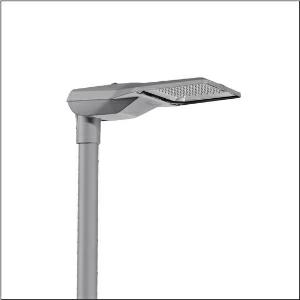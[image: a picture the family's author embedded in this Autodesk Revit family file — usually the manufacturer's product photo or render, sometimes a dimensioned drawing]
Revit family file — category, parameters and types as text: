
# Revit family: streetlight_sl_21_midi___pl52_5xe3h33s08lb_2890
name_source: partatom
category: Lighting Fixtures
units: mm (PartAtom-declared; Revit-internal decimal feet)

## family parameters
Cut with Voids When Loaded = No
Host = Face
Light Source = No
Part Type = Normal
Room Calculation Point = No
Round Connector Dimension = Use Diameter
Shared = No

## types (1)
- --- (1 x LED, 14100 lm, 98.3 W, 3000K)
    Apparent Load = 98 VA
    CIE Flux Codes = 27 59 98 100 100
    Color Rendering = 70
    Color Temperature = 3000K
    Default Elevation = 1800 mm
    Description = Streetlight SL 21 midi, mast luminaire, primary light control with lens, of PMMA, primary optical cover: cover, of toughened safety glass, transparent, light distribution: PL52, light emission: direct distribution, primary light characteristic: asymmetric, installation type: side-entry, post-top, LED, High Power LED, rated luminous flux: 14.100lm, luminous efficacy: 143lm/W, light colour: 730, colour temperature: 3000K, control: overheat protection, constant luminous flux control, time-dependent luminous flux control, flexible luminous flux parameterisation, presetting dimming logarithmic, mains connection: 230..240V, AC, 50/60Hz, start of lifetime: 98W, end of service life: 101W, reduction: 45W, luminaire housing, of diecast aluminium, powder-coated, Siteco® metallic grey (DB 702S), corrosivity category C5 mid according to DIN EN ISO 12944, please order mast flange separately, inclination adjustable: 0°, 5°, 10°, 15°, sealing non-destructively replaceable, multi-level sealing system, length: 644mm, width: 335mm, height: 110mm, mast flange for spigot size: 42mm (side-entry): 5XC10008XM4, 60/48mm (side-entry/post-top): 5XC10108XM2, 76/60mm (side-entry/post-top): 5XC10108XM1, Smart Interface above, protection rating (complete): IP66, insulation class (complete): insulation class II (safety insulation), certification: CE, ENEC, ENEC+, VDE, impact resistance: IK09, permissible operating ambient temperature for outdoor applications: -40..+50°C, standard-compliant lighting for roads and squares, packaging unit: 1 piece

Light Distribution: PL52
    Height = 111 mm
    Lamp = 1 x LED
    Lamp Light Flux = 14100 lm
    Lamp Power = 98.3 W
    Lamp count = 1
    Length = 644 mm
    Luminous efficacy = 143 lm/W
    Manufacturer = Siteco
    ModVariant = No
    Model = 5XE3H33S08LB
    Number of Poles = 1
    OnlyDefault = Yes
    Power Factor = 1
    Product Name = Streetlight SL 21 midi | PL52
    Product group = mast luminaire | pylon top
    ProductGroupID = 6100
    Protection Class = Protection class II
    Protection Degree = IP 66
    RLX_Detail_Level = 1
    RLX_Emergency_Light_Flux = 0 lm
    RLX_Emergency_Type = 0
    RLX_Emergency_Type_DB = No
    RlxData = <blob elided: 100449 chars, md5=0a31f778>
    Socket = socket
    Standby Power = 0 W
    System Light Flux = 14100 lm
    System Power = 98 W
    Type Comments = factory setting: luminous flux: 100 % | dim-lin: 254 | 1020 mA
    Type Image = l_1004302.jpg
    URL = http://relux.com
    VarID = @adj_143141
    Voltage = 0 V
    Weight = 0.00 kg
    Width = 336 mm

## geometry (parser evidence)
native form markers: Blend x4, Sweep x11
no freeform markers — native parametric forms only
